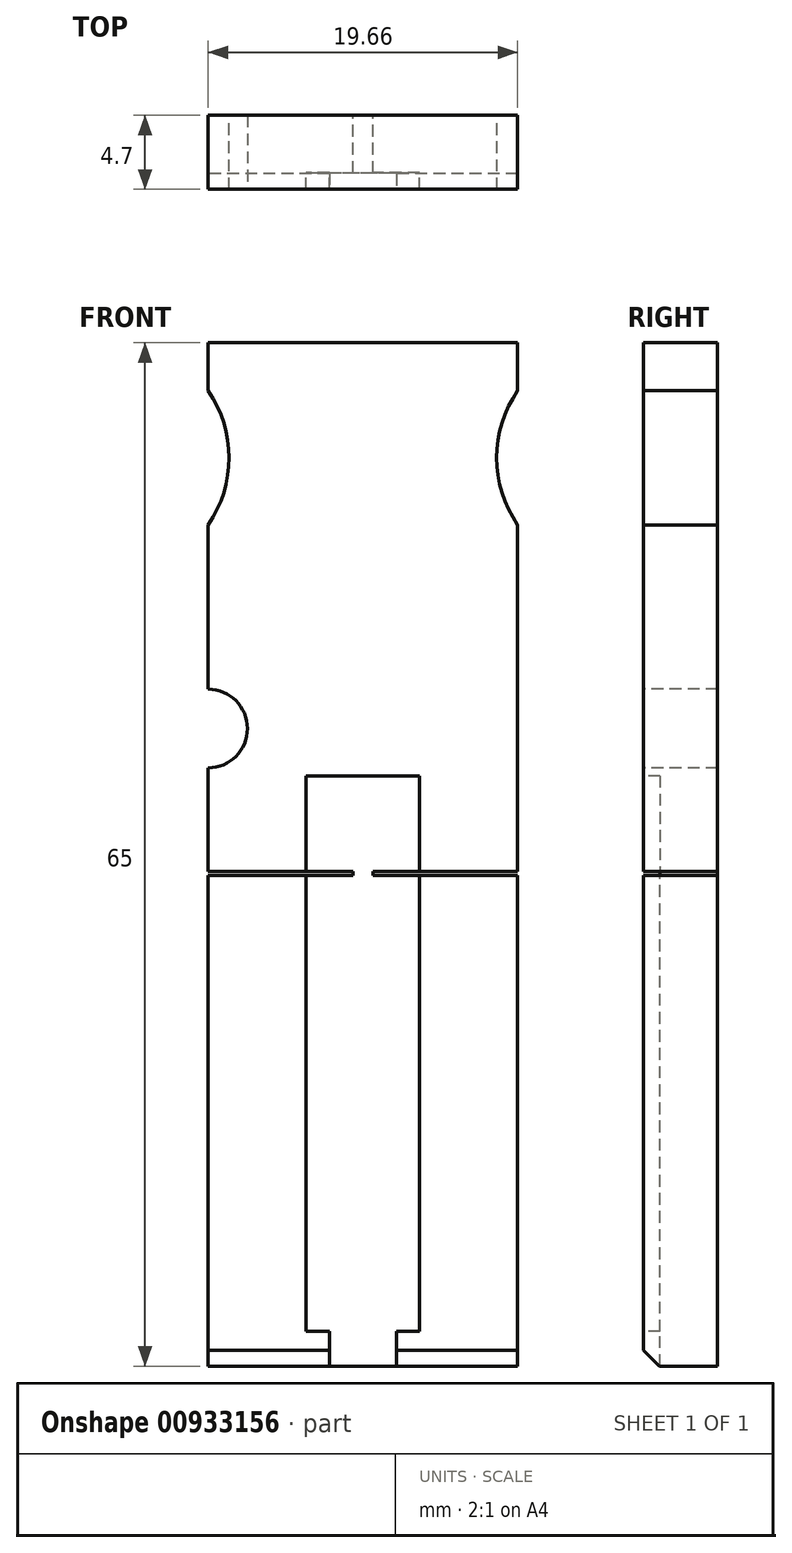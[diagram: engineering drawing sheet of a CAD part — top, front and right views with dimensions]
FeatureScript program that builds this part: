
annotation { "Feature Type Name" : "Feature", "Feature Type Description" : "" }
export const myFeature = defineFeature(function(context is Context, id is Id, definition is map)
    precondition{}
    {
        {
            var Q0;
            Q0=qCreatedBy(makeId("Front.planeOp"),FACE);
            var sketch = newSketch(context, id + "F0", { "sketchPlane" : qUnion([Q0])});
            skLineSegment(sketch, "E0.bottom", {"start": v(0, 0) * mm, "end": v(19.66, 0) * mm});
            skLineSegment(sketch, "E0.top", {"start": v(0, 65) * mm, "end": v(19.66, 65) * mm});
            skLineSegment(sketch, "E0.left", {"start": v(0, 0) * mm, "end": v(0, 65) * mm});
            skLineSegment(sketch, "E0.right", {"start": v(19.66, 0) * mm, "end": v(19.66, 65) * mm});
            skLineSegment(sketch, "E1", {"start": v(9.83, 65) * mm, "end": v(9.83, 0) * mm, "construction": true});
            skPoint(sketch, "E2", {"position": v(9.83, 38.5) * mm});
            skLineSegment(sketch, "E3", {"start": v(-8.64, 31.3) * mm, "end": v(33.92, 31.3) * mm, "construction": true});
            skLineSegment(sketch, "E4", {"start": v(0, 31.18) * mm, "end": v(0, 31.42) * mm});
            skCircle(sketch, "E5", {"center": v(25.83, 57.7) * mm, "radius": 7.5 * mm});
            skCircle(sketch, "E6.MirrorC", {"center": v(-6.17, 57.7) * mm, "radius": 7.5 * mm});
            skLineSegment(sketch, "E7.bottom", {"start": v(0, 31.42) * mm, "end": v(9.2, 31.42) * mm});
            skLineSegment(sketch, "E7.top", {"start": v(0, 31.42) * mm, "end": v(9.2, 31.42) * mm});
            skLineSegment(sketch, "E7.left", {"start": v(0, 31.42) * mm, "end": v(0, 31.42) * mm});
            skLineSegment(sketch, "E7.right", {"start": v(9.2, 31.42) * mm, "end": v(9.2, 31.42) * mm});
            skLineSegment(sketch, "E8", {"start": v(9.2, 31.42) * mm, "end": v(9.2, 31.18) * mm});
            skLineSegment(sketch, "E9", {"start": v(9.2, 31.18) * mm, "end": v(0, 31.18) * mm});
            skLineSegment(sketch, "E10", {"start": v(0, 31.42) * mm, "end": v(0, 31.18) * mm});
            skLineSegment(sketch, "E11.MirrorCS", {"start": v(19.66, 31.42) * mm, "end": v(10.46, 31.42) * mm});
            skLineSegment(sketch, "E12.MirrorCS", {"start": v(10.46, 31.42) * mm, "end": v(10.46, 31.18) * mm});
            skLineSegment(sketch, "E13.MirrorCS", {"start": v(10.46, 31.18) * mm, "end": v(19.66, 31.18) * mm});
            skLineSegment(sketch, "E14.MirrorCS", {"start": v(19.66, 31.42) * mm, "end": v(19.66, 31.18) * mm});
            skSolve(sketch);
        }
        {
            var Q0;
            {var subQ6=sQuery(id+"F0.wireOp",EDGE,"E0.bottom");Q0=makeQuery(id+"F0.imprint","IMPRINT",FACE,{"disambiguationData":[TD([[makeQuery(id+"F0.imprint","IMPRINT",EDGE,{"derivedFrom":subQ6}),1.0]])]});}
            extrude(context, id + "F1", {"entities" : qUnion([Q0]), "depth" : 4.7 * mm, "offsetDistance" : 25 * mm});
        }
        {
            var Q0;
            Q0=makeQuery(id+"F1.opExtrude","CAP_FACE",FACE,{"disambiguationData":[OSD([sQuery(id+"F0.wireOp",EDGE,"E0.bottom"),sQuery(id+"F0.wireOp",EDGE,"E0.top"),sQuery(id+"F0.wireOp",EDGE,"E0.left"),sQuery(id+"F0.wireOp",EDGE,"E0.right"),sQuery(id+"F0.wireOp",EDGE,"E5"),sQuery(id+"F0.wireOp",EDGE,"E6.MirrorC"),sQuery(id+"F0.wireOp",EDGE,"E7.bottom"),sQuery(id+"F0.wireOp",EDGE,"E8"),sQuery(id+"F0.wireOp",EDGE,"E9"),sQuery(id+"F0.wireOp",EDGE,"E11.MirrorCS"),sQuery(id+"F0.wireOp",EDGE,"E12.MirrorCS"),sQuery(id+"F0.wireOp",EDGE,"E13.MirrorCS")])],"isStart":false});
            var sketch = newSketch(context, id + "F2", { "sketchPlane" : qUnion([Q0])});
            skLineSegment(sketch, "E15", {"start": v(6.23, 37.5) * mm, "end": v(13.43, 37.5) * mm});
            skLineSegment(sketch, "E16", {"start": v(13.43, 37.5) * mm, "end": v(13.43, 2.2) * mm});
            skLineSegment(sketch, "E17", {"start": v(13.43, 2.2) * mm, "end": v(11.95, 2.2) * mm});
            skLineSegment(sketch, "E18", {"start": v(11.95, 2.2) * mm, "end": v(11.95, 0) * mm});
            skLineSegment(sketch, "E19", {"start": v(11.95, 0) * mm, "end": v(7.7, 0) * mm});
            skLineSegment(sketch, "E20", {"start": v(7.7, 0) * mm, "end": v(7.7, 2.2) * mm});
            skLineSegment(sketch, "E21", {"start": v(7.7, 2.2) * mm, "end": v(6.23, 2.2) * mm});
            skLineSegment(sketch, "E22", {"start": v(6.23, 2.2) * mm, "end": v(6.23, 37.5) * mm});
            skLineSegment(sketch, "E23", {"start": v(9.83, 65) * mm, "end": v(9.83, 0) * mm, "construction": true});
            skSolve(sketch);
        }
        {
            var Q0;
            Q0 = qSketchRegion(id + "F2", true);
            extrude(context, id + "F3", {"entities" : qUnion([Q0]), "operationType" : NewBodyOperationType.REMOVE, "oppositeDirection" : true, "depth" : 1.05 * mm, "offsetDistance" : 25 * mm});
        }
        {
            var Q0;
            {var subQ0=sQuery(id+"F0.wireOp",EDGE,"E0.bottom");Q0=makeQuery(id+"F3.boolean.opBoolean","SPLIT",EDGE,{"disambiguationData":[TD([makeQuery(id+"F3.opExtrude","SWEPT_FACE",FACE,{"disambiguationData":[OSD([sQuery(id+"F2.wireOp",EDGE,"E18")])]})])],"derivedFrom":makeQuery(id+"F1.opExtrude","CAP_EDGE",EDGE,{"disambiguationData":[OSD([subQ0])],"isStart":false})});}
            var Q1;
            {var subQ0=sQuery(id+"F0.wireOp",EDGE,"E0.bottom");Q1=makeQuery(id+"F3.boolean.opBoolean","SPLIT",EDGE,{"disambiguationData":[TD([makeQuery(id+"F3.opExtrude","SWEPT_FACE",FACE,{"disambiguationData":[OSD([sQuery(id+"F2.wireOp",EDGE,"E20")])]})])],"derivedFrom":makeQuery(id+"F1.opExtrude","CAP_EDGE",EDGE,{"disambiguationData":[OSD([subQ0])],"isStart":false})});}
            chamfer(context, id + "F4", {"entities" : qUnion([Q0, Q1]), "width" : 1 * mm, "tangentPropagation" : true});
        }
        {
            var Q0;
            {var subQ0=sQuery(id+"F0.wireOp",EDGE,"E0.right");Q0=qUnion([makeQuery(id+"F1.opExtrude","SWEPT_FACE",FACE,{"disambiguationData":[OSD([subQ0]),TDD([makeQuery(id+"F0.imprint","IMPRINT",EDGE,{"disambiguationData":[TD([[makeQuery(id+"F0.imprint","INTERSECT",VERTEX,{"derivedFrom":[subQ0,sQuery(id+"F0.wireOp",EDGE,"E11.MirrorCS")]}),-1.0]])],"derivedFrom":subQ0})])]}),makeQuery(id+"F1.opExtrude","SWEPT_FACE",FACE,{"disambiguationData":[OSD([subQ0]),TDD([makeQuery(id+"F0.imprint","IMPRINT",EDGE,{"disambiguationData":[TD([[makeQuery(id+"F0.imprint","INTERSECT",VERTEX,{"derivedFrom":[sQuery(id+"F0.wireOp",EDGE,"E0.bottom"),subQ0]}),-1.0]])],"derivedFrom":subQ0})])]}),makeQuery(id+"F1.opExtrude","SWEPT_FACE",FACE,{"disambiguationData":[OSD([subQ0]),TDD([makeQuery(id+"F0.imprint","IMPRINT",EDGE,{"disambiguationData":[TD([[makeQuery(id+"F0.imprint","INTERSECT",VERTEX,{"derivedFrom":[sQuery(id+"F0.wireOp",EDGE,"E0.top"),subQ0]}),1.0]])],"derivedFrom":subQ0})])]})]);}
            var sketch = newSketch(context, id + "F5", { "sketchPlane" : qUnion([Q0])});
            skLineSegment(sketch, "E24", {"start": v(-15.64, 31.3) * mm, "end": v(17.74, 31.3) * mm, "construction": true});
            skLineSegment(sketch, "E25", {"start": v(-1, 31.3) * mm, "end": v(0, 32.3) * mm});
            skLineSegment(sketch, "E26", {"start": v(0, 32.3) * mm, "end": v(0, 30.3) * mm});
            skLineSegment(sketch, "E27", {"start": v(0, 30.3) * mm, "end": v(-1, 31.3) * mm});
            skSolve(sketch);
        }
        {
            var Q0;
            {var subQ0=sQuery(id+"F0.wireOp",EDGE,"E11.MirrorCS");var subQ1=sQuery(id+"F0.wireOp",EDGE,"E7.bottom");var subQ2=sQuery(id+"F0.wireOp",EDGE,"E6.MirrorC");var subQ3=sQuery(id+"F0.wireOp",EDGE,"E5");var subQ4=sQuery(id+"F0.wireOp",EDGE,"E0.right");var subQ5=sQuery(id+"F0.wireOp",EDGE,"E0.top");var subQ6=sQuery(id+"F0.wireOp",EDGE,"E0.left");var subQ9=sQuery(id+"F0.wireOp",EDGE,"E13.MirrorCS");var subQ10=sQuery(id+"F0.wireOp",EDGE,"E9");var subQ11=sQuery(id+"F0.wireOp",EDGE,"E0.bottom");var subQ12=makeQuery(id+"F1.opExtrude","CAP_FACE",FACE,{"disambiguationData":[OSD([subQ11,subQ5,subQ6,subQ4,subQ3,subQ2,subQ1,sQuery(id+"F0.wireOp",EDGE,"E8"),subQ10,subQ0,sQuery(id+"F0.wireOp",EDGE,"E12.MirrorCS"),subQ9])],"isStart":false});Q0=qUnion([makeQuery(id+"F3.boolean.opBoolean","SPLIT",FACE,{"disambiguationData":[TD([makeQuery(id+"F1.opExtrude","SWEPT_FACE",FACE,{"disambiguationData":[OSD([subQ10])]})])],"derivedFrom":subQ12}),makeQuery(id+"F3.boolean.opBoolean","SPLIT",FACE,{"disambiguationData":[TD([makeQuery(id+"F1.opExtrude","SWEPT_FACE",FACE,{"disambiguationData":[OSD([subQ9])]})])],"derivedFrom":subQ12}),makeQuery(id+"F3.boolean.opBoolean","SPLIT",FACE,{"disambiguationData":[TD([makeQuery(id+"F1.opExtrude","SWEPT_FACE",FACE,{"disambiguationData":[OSD([subQ5])]})])],"derivedFrom":subQ12})]);}
            var sketch = newSketch(context, id + "F6", { "sketchPlane" : qUnion([Q0])});
            skPoint(sketch, "E28", {"position": v(0, 40.5) * mm});
            skSolve(sketch);
        }
        {
            var Q0;
            Q0=sQuery(id+"F6.wireOp",VERTEX,"E28");
            var Q1;
            Q1=makeQuery(id+"F1.opExtrude","SWEPT_BODY",BODY,{"disambiguationData":[OSD([sQuery(id+"F0.wireOp",EDGE,"E0.bottom"),sQuery(id+"F0.wireOp",EDGE,"E0.top"),sQuery(id+"F0.wireOp",EDGE,"E0.left"),sQuery(id+"F0.wireOp",EDGE,"E0.right"),sQuery(id+"F0.wireOp",EDGE,"E5"),sQuery(id+"F0.wireOp",EDGE,"E6.MirrorC"),sQuery(id+"F0.wireOp",EDGE,"E7.bottom"),sQuery(id+"F0.wireOp",EDGE,"E8"),sQuery(id+"F0.wireOp",EDGE,"E9"),sQuery(id+"F0.wireOp",EDGE,"E11.MirrorCS"),sQuery(id+"F0.wireOp",EDGE,"E12.MirrorCS"),sQuery(id+"F0.wireOp",EDGE,"E13.MirrorCS")])]});
            hole(context, id + "F7", {"style" : HoleStyle.SIMPLE, "endStyle" : HoleEndStyle.THROUGH, "holeDiameter" : 5 * mm, "majorDiameter" : 5 * mm, "isTappedThrough" : true, "tappedDepth" : 12 * mm, "tapClearance" : 3, "locations" : qUnion([Q0]), "scope" : qUnion([Q1])});
        }
    });
